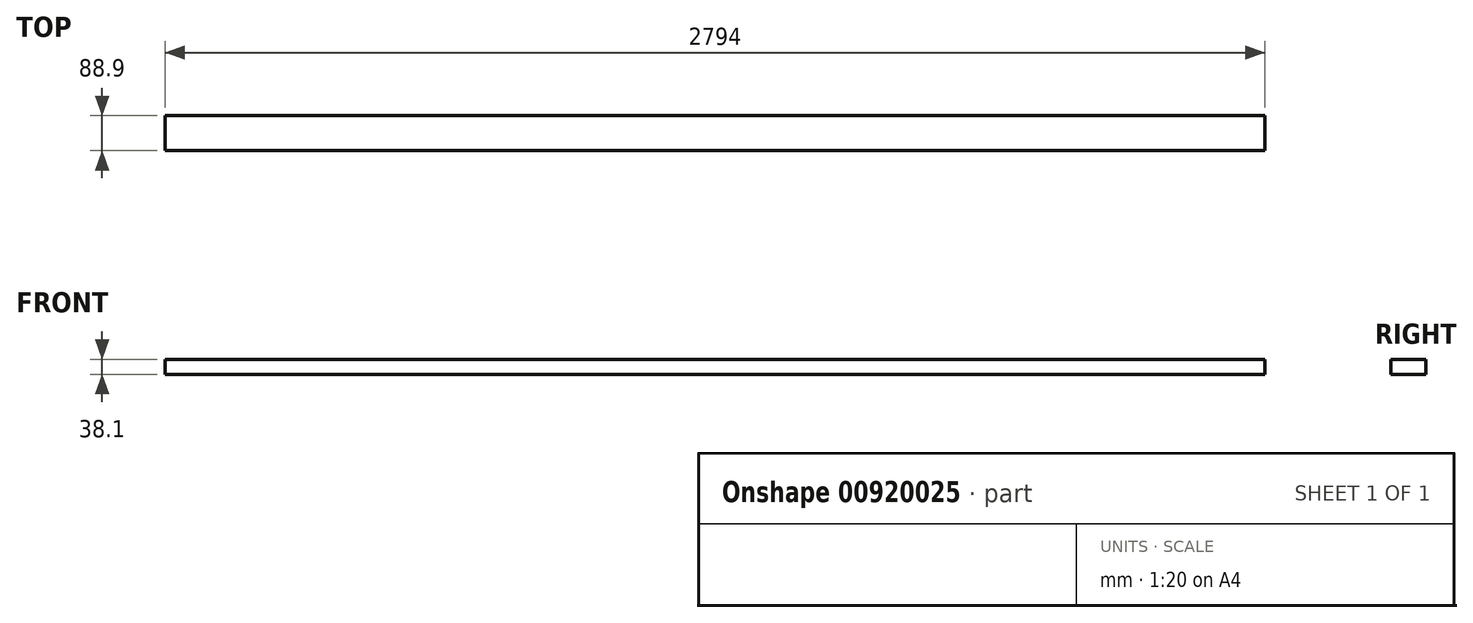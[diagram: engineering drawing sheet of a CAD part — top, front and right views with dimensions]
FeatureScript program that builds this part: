
annotation { "Feature Type Name" : "Feature", "Feature Type Description" : "" }
export const myFeature = defineFeature(function(context is Context, id is Id, definition is map)
    precondition{}
    {
        {
            var Q0;
            Q0=qCreatedBy(makeId("Right.planeOp"),FACE);
            var sketch = newSketch(context, id + "F0", { "sketchPlane" : qUnion([Q0])});
            skLineSegment(sketch, "E0.bottom", {"start": v(44.45, 19.05) * mm, "end": v(-44.45, 19.05) * mm});
            skLineSegment(sketch, "E0.top", {"start": v(44.45, -19.05) * mm, "end": v(-44.45, -19.05) * mm});
            skLineSegment(sketch, "E0.left", {"start": v(44.45, 19.05) * mm, "end": v(44.45, -19.05) * mm});
            skLineSegment(sketch, "E0.right", {"start": v(-44.45, 19.05) * mm, "end": v(-44.45, -19.05) * mm});
            skPoint(sketch, "E0.middle", {"position": v(0, 0) * mm});
            skSolve(sketch);
        }
        {
            var Q0;
            Q0 = qSketchRegion(id + "F0", true);
            extrude(context, id + "F1", {"entities" : qUnion([Q0]), "oppositeDirection" : true, "depth" : 2794 * mm, "offsetDistance" : 25.4 * mm});
        }
    });
